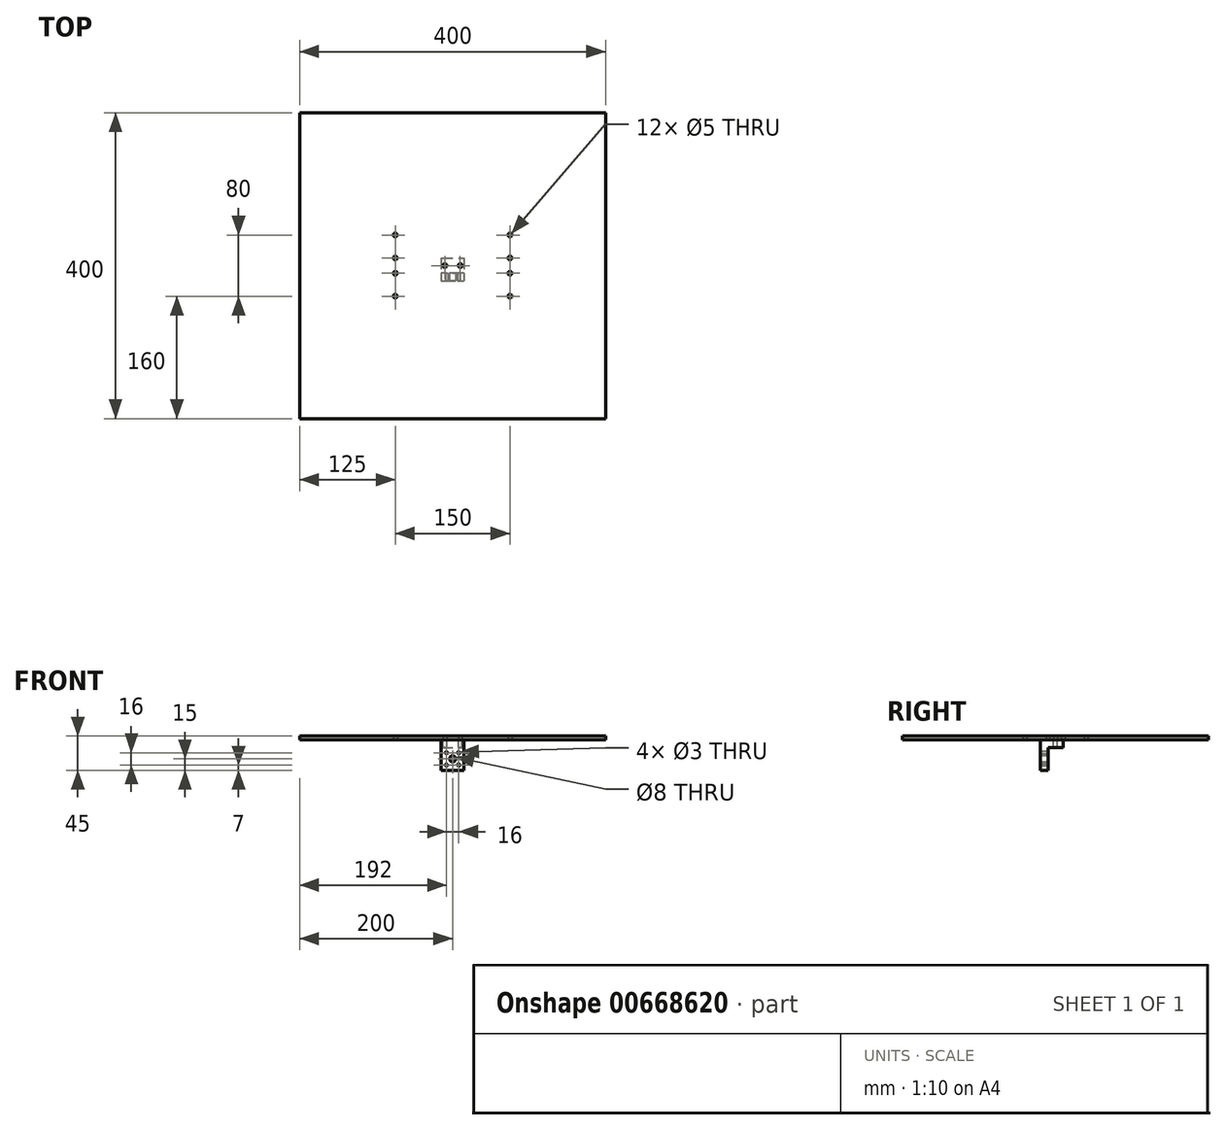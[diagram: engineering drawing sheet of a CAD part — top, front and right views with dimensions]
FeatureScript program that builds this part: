
annotation { "Feature Type Name" : "Feature", "Feature Type Description" : "" }
export const myFeature = defineFeature(function(context is Context, id is Id, definition is map)
    precondition{}
    {
        {
            var Q0;
            Q0=qCreatedBy(makeId("Top.planeOp"),FACE);
            var sketch = newSketch(context, id + "F0", { "sketchPlane" : qUnion([Q0])});
            skLineSegment(sketch, "E0.bottom", {"start": v(-200, 200) * mm, "end": v(200, 200) * mm});
            skLineSegment(sketch, "E0.top", {"start": v(-200, -200) * mm, "end": v(200, -200) * mm});
            skLineSegment(sketch, "E0.left", {"start": v(-200, 200) * mm, "end": v(-200, -200) * mm});
            skLineSegment(sketch, "E0.right", {"start": v(200, 200) * mm, "end": v(200, -200) * mm});
            skPoint(sketch, "E0.middle", {"position": v(0, 0) * mm});
            skPoint(sketch, "E1", {"position": v(-75, -10) * mm});
            skPoint(sketch, "E2", {"position": v(-75, -40) * mm});
            skPoint(sketch, "E3.0.1.0", {"position": v(-75, 40) * mm});
            skPoint(sketch, "E3.0.1.1", {"position": v(-75, 10) * mm});
            skPoint(sketch, "E3.1.0.0", {"position": v(75, -10) * mm});
            skPoint(sketch, "E3.1.0.1", {"position": v(75, -40) * mm});
            skPoint(sketch, "E3.1.1.0", {"position": v(75, 40) * mm});
            skPoint(sketch, "E3.1.1.1", {"position": v(75, 10) * mm});
            skLineSegment(sketch, "E3.direction1", {"start": v(-75, -40) * mm, "end": v(75, -40) * mm, "construction": true});
            skLineSegment(sketch, "E3.direction2", {"start": v(-75, -40) * mm, "end": v(-75, 10) * mm, "construction": true});
            skSolve(sketch);
        }
        {
            var Q0;
            Q0=qSketchRegion(id+"F0",true);
            extrude(context, id + "F1", {"entities" : qUnion([Q0]), "depth" : 5 * mm});
        }
        {
            var Q0;
            Q0=makeQuery(id+"F0.imprint","IMPRINT",FACE,{"disambiguationData":[TD([[makeQuery(id+"F0.imprint","IMPRINT",EDGE,{"derivedFrom":sQuery(id+"F0.wireOp",EDGE,"E0.bottom")}),-1.0]])]});
            var sketch = newSketch(context, id + "F2", { "sketchPlane" : qUnion([Q0])});
            skPoint(sketch, "E4.middle", {"position": v(0, 0) * mm});
            skPoint(sketch, "E5", {"position": v(-10, 0) * mm});
            skPoint(sketch, "E6", {"position": v(10, 0) * mm});
            skSolve(sketch);
        }
        {
            var Q0;
            Q0=sQuery(id+"F0.wireOp",VERTEX,"E2");
            var Q1;
            Q1=sQuery(id+"F0.wireOp",VERTEX,"E1");
            var Q2;
            Q2=sQuery(id+"F0.wireOp",VERTEX,"E3.0.1.1");
            var Q3;
            Q3=sQuery(id+"F0.wireOp",VERTEX,"E3.0.1.0");
            var Q4;
            Q4=sQuery(id+"F0.wireOp",VERTEX,"E3.1.0.1");
            var Q5;
            Q5=sQuery(id+"F0.wireOp",VERTEX,"E3.1.0.0");
            var Q6;
            Q6=sQuery(id+"F0.wireOp",VERTEX,"E3.1.1.1");
            var Q7;
            Q7=sQuery(id+"F0.wireOp",VERTEX,"E3.1.1.0");
            var Q8;
            Q8=sQuery(id+"F2.wireOp",VERTEX,"E5");
            var Q9;
            Q9=sQuery(id+"F2.wireOp",VERTEX,"E6");
            var Q10;
            Q10=makeQuery(id+"F1.opExtrude","SWEPT_BODY",BODY,{"disambiguationData":[OSD([sQuery(id+"F0.wireOp",EDGE,"E0.bottom"),sQuery(id+"F0.wireOp",EDGE,"E0.top"),sQuery(id+"F0.wireOp",EDGE,"E0.left"),sQuery(id+"F0.wireOp",EDGE,"E0.right")])]});
            hole(context, id + "F3", {"style" : HoleStyle.SIMPLE, "endStyle" : HoleEndStyle.THROUGH, "oppositeDirection" : true, "holeDiameter" : 5 * mm, "isTappedThrough" : true, "tappedDepth" : 12 * mm, "tapClearance" : 3, "locations" : qUnion([Q0, Q1, Q2, Q3, Q4, Q5, Q6, Q7, Q8, Q9]), "scope" : qUnion([Q10])});
        }
        {
            var Q0;
            Q0=makeQuery(id+"F0.imprint","IMPRINT",FACE,{"disambiguationData":[TD([[makeQuery(id+"F0.imprint","IMPRINT",EDGE,{"derivedFrom":sQuery(id+"F0.wireOp",EDGE,"E0.bottom")}),-1.0]])]});
            var sketch = newSketch(context, id + "F4", { "sketchPlane" : qUnion([Q0])});
            skLineSegment(sketch, "E7.bottom", {"start": v(-15, 10) * mm, "end": v(15, 10) * mm});
            skLineSegment(sketch, "E7.top", {"start": v(-15, -20) * mm, "end": v(15, -20) * mm});
            skLineSegment(sketch, "E7.left", {"start": v(-15, 10) * mm, "end": v(-15, -20) * mm});
            skLineSegment(sketch, "E7.right", {"start": v(15, 10) * mm, "end": v(15, -20) * mm});
            skPoint(sketch, "E7.middle", {"position": v(0, 0) * mm});
            skCircle(sketch, "E8", {"center": v(-10, 0) * mm, "radius": 2.5 * mm});
            skCircle(sketch, "E9", {"center": v(10, 0) * mm, "radius": 2.5 * mm});
            skSolve(sketch);
        }
        {
            var Q0;
            Q0=qSketchRegion(id+"F4",true);
            extrude(context, id + "F5", {"entities" : qUnion([Q0]), "oppositeDirection" : true, "depth" : 10 * mm});
        }
        {
            var Q0;
            Q0=makeQuery(id+"F5.opExtrude","CAP_FACE",FACE,{"disambiguationData":[OSD([sQuery(id+"F4.wireOp",EDGE,"E7.bottom"),sQuery(id+"F4.wireOp",EDGE,"E7.top"),sQuery(id+"F4.wireOp",EDGE,"E7.left"),sQuery(id+"F4.wireOp",EDGE,"E7.right")])],"isStart":false});
            var sketch = newSketch(context, id + "F6", { "sketchPlane" : qUnion([Q0])});
            skLineSegment(sketch, "E10.bottom", {"start": v(15, 10) * mm, "end": v(-15, 10) * mm});
            skLineSegment(sketch, "E10.top", {"start": v(15, 20) * mm, "end": v(-15, 20) * mm});
            skLineSegment(sketch, "E10.left", {"start": v(15, 10) * mm, "end": v(15, 20) * mm});
            skLineSegment(sketch, "E10.right", {"start": v(-15, 10) * mm, "end": v(-15, 20) * mm});
            skSolve(sketch);
        }
        {
            var Q0;
            Q0=qSketchRegion(id+"F6",true);
            extrude(context, id + "F7", {"entities" : qUnion([Q0]), "operationType" : NewBodyOperationType.ADD, "depth" : 30 * mm});
        }
        {
            var Q0;
            Q0=makeQuery(id+"F7.boolean.opBoolean","MERGE",FACE,{"derivedFrom":[makeQuery(id+"F5.opExtrude","SWEPT_FACE",FACE,{"disambiguationData":[OSD([sQuery(id+"F4.wireOp",EDGE,"E7.top")])]}),makeQuery(id+"F7.opExtrude","SWEPT_FACE",FACE,{"disambiguationData":[OSD([sQuery(id+"F6.wireOp",EDGE,"E10.top")])]})]});
            var sketch = newSketch(context, id + "F8", { "sketchPlane" : qUnion([Q0])});
            skPoint(sketch, "E11", {"position": v(0, -25) * mm});
            skPoint(sketch, "E12", {"position": v(-8, -17) * mm});
            skLineSegment(sketch, "E13", {"start": v(-8, -17) * mm, "end": v(0, -17) * mm, "construction": true});
            skLineSegment(sketch, "E14", {"start": v(-8, -17) * mm, "end": v(-8, -25) * mm, "construction": true});
            skLineSegment(sketch, "E15", {"start": v(-8, -25) * mm, "end": v(0, -25) * mm, "construction": true});
            skPoint(sketch, "E16.0.1.0", {"position": v(-8, -33) * mm});
            skPoint(sketch, "E16.1.0.0", {"position": v(8, -17) * mm});
            skPoint(sketch, "E16.1.1.0", {"position": v(8, -33) * mm});
            skLineSegment(sketch, "E16.direction1", {"start": v(-8, -17) * mm, "end": v(8, -17) * mm, "construction": true});
            skLineSegment(sketch, "E16.direction2", {"start": v(-8, -17) * mm, "end": v(-8, -33) * mm, "construction": true});
            skCircle(sketch, "E17", {"center": v(0, -25) * mm, "radius": 15 * mm});
            skSolve(sketch);
        }
        {
            var Q0;
            Q0=sQuery(id+"F8.wireOp",VERTEX,"E12");
            var Q1;
            Q1=sQuery(id+"F8.wireOp",VERTEX,"E16.0.1.0");
            var Q2;
            Q2=sQuery(id+"F8.wireOp",VERTEX,"E16.1.0.0");
            var Q3;
            Q3=sQuery(id+"F8.wireOp",VERTEX,"E16.1.1.0");
            var Q4;
            Q4=makeQuery(id+"F5.opExtrude","SWEPT_BODY",BODY,{"disambiguationData":[OSD([sQuery(id+"F4.wireOp",EDGE,"E7.bottom"),sQuery(id+"F4.wireOp",EDGE,"E7.top"),sQuery(id+"F4.wireOp",EDGE,"E7.left"),sQuery(id+"F4.wireOp",EDGE,"E7.right")])]});
            hole(context, id + "F9", {"style" : HoleStyle.SIMPLE, "endStyle" : HoleEndStyle.THROUGH, "holeDiameter" : 3 * mm, "isTappedThrough" : true, "tappedDepth" : 12 * mm, "tapClearance" : 3, "locations" : qUnion([Q0, Q1, Q2, Q3]), "scope" : qUnion([Q4])});
        }
        {
            var Q0;
            Q0=sQuery(id+"F8.wireOp",VERTEX,"E11");
            var Q1;
            Q1=makeQuery(id+"F5.opExtrude","SWEPT_BODY",BODY,{"disambiguationData":[OSD([sQuery(id+"F4.wireOp",EDGE,"E7.bottom"),sQuery(id+"F4.wireOp",EDGE,"E7.top"),sQuery(id+"F4.wireOp",EDGE,"E7.left"),sQuery(id+"F4.wireOp",EDGE,"E7.right")])]});
            hole(context, id + "F10", {"style" : HoleStyle.SIMPLE, "endStyle" : HoleEndStyle.THROUGH, "holeDiameter" : 8 * mm, "isTappedThrough" : true, "tappedDepth" : 12 * mm, "tapClearance" : 3, "locations" : qUnion([Q0]), "scope" : qUnion([Q1])});
        }
    });
